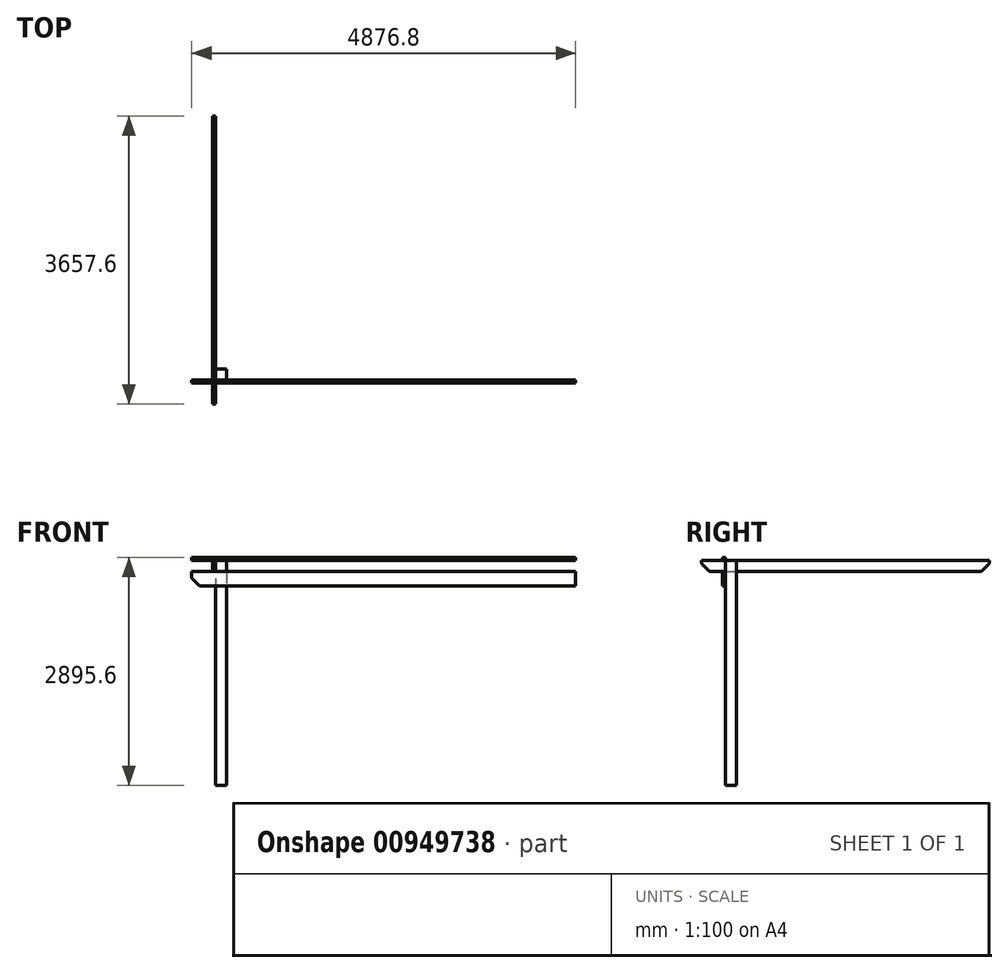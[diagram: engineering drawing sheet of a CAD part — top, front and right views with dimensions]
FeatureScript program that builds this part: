
annotation { "Feature Type Name" : "Feature", "Feature Type Description" : "" }
export const myFeature = defineFeature(function(context is Context, id is Id, definition is map)
    precondition{}
    {
        {
            var Q0;
            Q0=qCreatedBy(makeId("Top.planeOp"),FACE);
            var sketch = newSketch(context, id + "F0", { "sketchPlane" : qUnion([Q0])});
            skLineSegment(sketch, "E0.bottom", {"start": v(0, 139.7) * mm, "end": v(139.7, 139.7) * mm});
            skLineSegment(sketch, "E0.top", {"start": v(0, 0) * mm, "end": v(139.7, 0) * mm});
            skLineSegment(sketch, "E0.left", {"start": v(0, 139.7) * mm, "end": v(0, 0) * mm});
            skLineSegment(sketch, "E0.right", {"start": v(139.7, 139.7) * mm, "end": v(139.7, 0) * mm});
            skSolve(sketch);
        }
        {
            var Q0;
            Q0=makeQuery(id+"F0.imprint","IMPRINT",FACE,{"disambiguationData":[TD([[makeQuery(id+"F0.imprint","IMPRINT",EDGE,{"derivedFrom":sQuery(id+"F0.wireOp",EDGE,"E0.bottom")}),-1.0]])]});
            extrude(context, id + "F1", {"entities" : qUnion([Q0]), "depth" : 2438.4 * mm + 419.1 * mm, "offsetDistance" : 25.4 * mm});
        }
        {
            var Q0;
            Q0=makeQuery(id+"F1.opExtrude","SWEPT_FACE",FACE,{"disambiguationData":[OSD([sQuery(id+"F0.wireOp",EDGE,"E0.top")])]});
            var sketch = newSketch(context, id + "F2", { "sketchPlane" : qUnion([Q0])});
            skLineSegment(sketch, "E1.0", {"start": v(0, 2857.5) * mm, "end": v(139.7, 2857.5) * mm, "construction": true});
            skLineSegment(sketch, "E2.bottom", {"start": v(-304.8, 2717.8) * mm, "end": v(4572, 2717.8) * mm});
            skLineSegment(sketch, "E2.top", {"start": v(-304.8, 2533.65) * mm, "end": v(4572, 2533.65) * mm});
            skLineSegment(sketch, "E2.left", {"start": v(-304.8, 2717.8) * mm, "end": v(-304.8, 2533.65) * mm});
            skLineSegment(sketch, "E2.right", {"start": v(4572, 2717.8) * mm, "end": v(4572, 2533.65) * mm});
            skSolve(sketch);
        }
        {
            var Q0;
            Q0 = qSketchRegion(id + "F2", true);
            extrude(context, id + "F3", {"entities" : qUnion([Q0]), "depth" : 38.1 * mm, "offsetDistance" : 25.4 * mm});
        }
        {
            var Q0;
            Q0=makeQuery(id+"F3.opExtrude","SWEPT_EDGE",EDGE,{"disambiguationData":[OSD([sQuery(id+"F2.wireOp",EDGE,"E2.top"),sQuery(id+"F2.wireOp",EDGE,"E2.left")])]});
            chamfer(context, id + "F4", {"entities" : qUnion([Q0]), "width" : 101.6 * mm, "tangentPropagation" : true});
        }
        {
            var Q0;
            Q0=qCreatedBy(makeId("Right.planeOp"),FACE);
            var sketch = newSketch(context, id + "F5", { "sketchPlane" : qUnion([Q0])});
            skLineSegment(sketch, "E3.0", {"start": v(139.7, 2857.5) * mm, "end": v(0, 2857.5) * mm, "construction": true});
            skLineSegment(sketch, "E4.bottom", {"start": v(-304.8, 2857.5) * mm, "end": v(3352.8, 2857.5) * mm});
            skLineSegment(sketch, "E4.top", {"start": v(-304.8, 2717.8) * mm, "end": v(3352.8, 2717.8) * mm});
            skLineSegment(sketch, "E4.left", {"start": v(-304.8, 2857.5) * mm, "end": v(-304.8, 2717.8) * mm});
            skLineSegment(sketch, "E4.right", {"start": v(3352.8, 2857.5) * mm, "end": v(3352.8, 2717.8) * mm});
            skLineSegment(sketch, "E5.0.1", {"start": v(0, 2717.8) * mm, "end": v(-38.1, 2717.8) * mm});
            skLineSegment(sketch, "E5.0.3", {"start": v(-38.1, 2717.8) * mm, "end": v(0, 2717.8) * mm, "construction": true});
            skSolve(sketch);
        }
        {
            var Q0;
            Q0=makeQuery(id+"F5.imprint","IMPRINT",FACE,{"disambiguationData":[TD([[makeQuery(id+"F5.imprint","IMPRINT",EDGE,{"derivedFrom":sQuery(id+"F5.wireOp",EDGE,"E4.bottom")}),-1.0]])]});
            extrude(context, id + "F6", {"entities" : qUnion([Q0]), "oppositeDirection" : true, "depth" : 38.1 * mm, "offsetDistance" : 25.4 * mm});
        }
        {
            var Q0;
            Q0=makeQuery(id+"F6.opExtrude","SWEPT_EDGE",EDGE,{"disambiguationData":[OSD([sQuery(id+"F5.wireOp",EDGE,"E4.top"),sQuery(id+"F5.wireOp",EDGE,"E4.left")])]});
            var Q1;
            Q1=makeQuery(id+"F6.opExtrude","SWEPT_EDGE",EDGE,{"disambiguationData":[OSD([sQuery(id+"F5.wireOp",EDGE,"E4.top"),sQuery(id+"F5.wireOp",EDGE,"E4.right")])]});
            chamfer(context, id + "F7", {"entities" : qUnion([Q0, Q1]), "width" : 101.6 * mm, "tangentPropagation" : true});
        }
        {
            var Q0;
            Q0=qCreatedBy(makeId("Front.planeOp"),FACE);
            var sketch = newSketch(context, id + "F8", { "sketchPlane" : qUnion([Q0])});
            skLineSegment(sketch, "E6.bottom", {"start": v(-304.8, 2895.6) * mm, "end": v(4572, 2895.6) * mm});
            skLineSegment(sketch, "E6.top", {"start": v(-304.8, 2857.5) * mm, "end": v(4572, 2857.5) * mm});
            skLineSegment(sketch, "E6.left", {"start": v(-304.8, 2895.6) * mm, "end": v(-304.8, 2857.5) * mm});
            skLineSegment(sketch, "E6.right", {"start": v(4572, 2895.6) * mm, "end": v(4572, 2857.5) * mm});
            skSolve(sketch);
        }
        {
            var Q0;
            Q0=makeQuery(id+"F8.imprint","IMPRINT",FACE,{"disambiguationData":[TD([[makeQuery(id+"F8.imprint","IMPRINT",EDGE,{"derivedFrom":sQuery(id+"F8.wireOp",EDGE,"E6.bottom")}),-1.0]])]});
            extrude(context, id + "F9", {"entities" : qUnion([Q0]), "depth" : 38.1 * mm, "offsetDistance" : 25.4 * mm});
        }
    });
